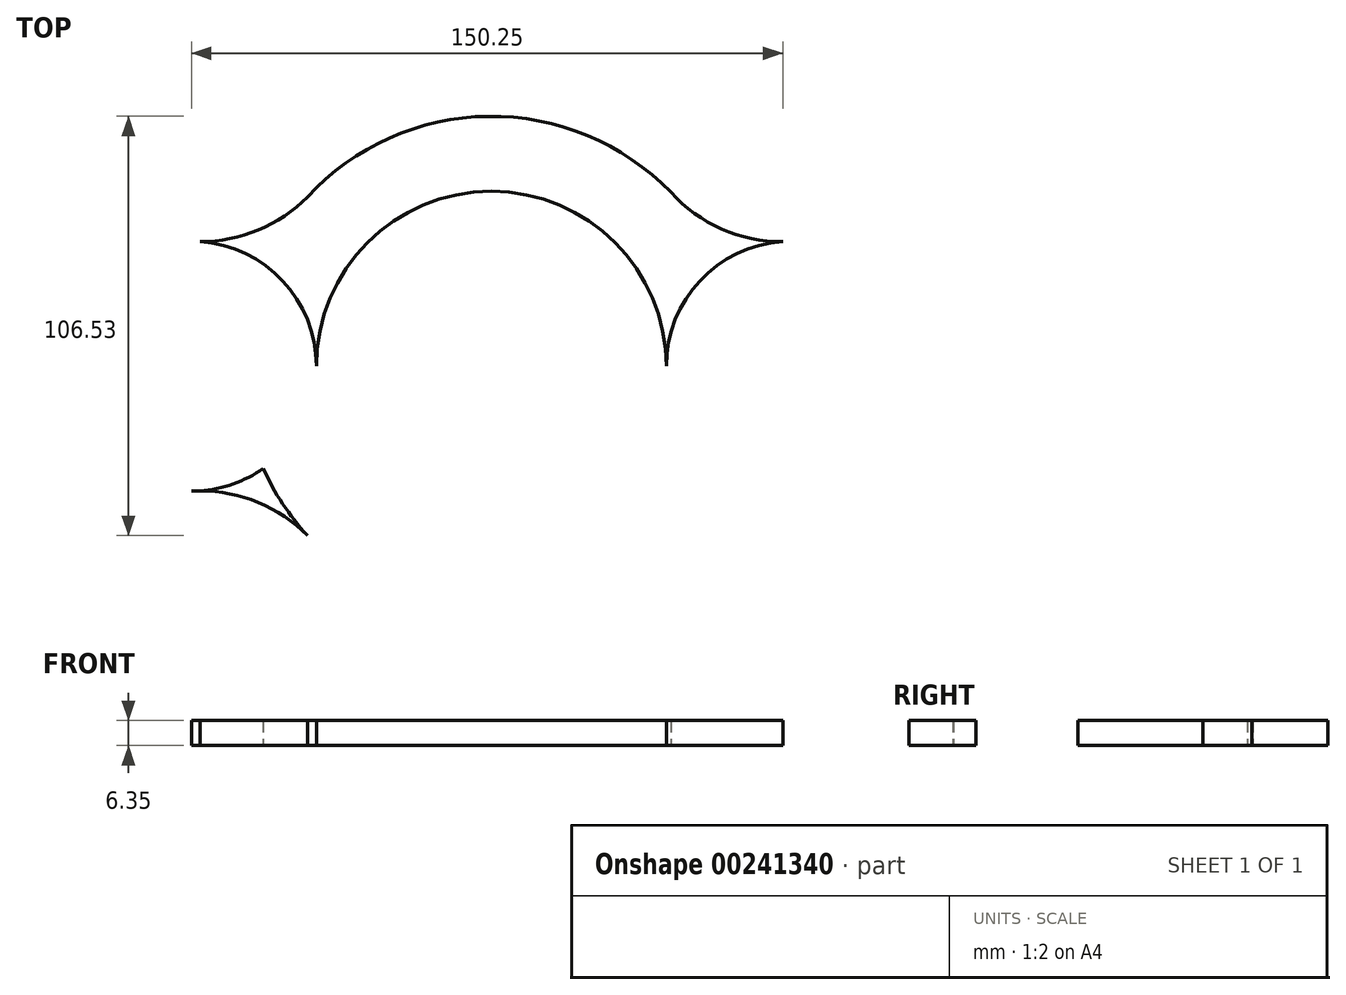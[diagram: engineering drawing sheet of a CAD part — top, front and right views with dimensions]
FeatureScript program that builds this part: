
annotation { "Feature Type Name" : "Feature", "Feature Type Description" : "" }
export const myFeature = defineFeature(function(context is Context, id is Id, definition is map)
    precondition{}
    {
        {
            var Q0;
            Q0=qCreatedBy(makeId("Top.planeOp"),FACE);
            var sketch = newSketch(context, id + "F0", { "sketchPlane" : qUnion([Q0])});
            skCircle(sketch, "E0", {"center": v(0, 0) * mm, "radius": 44.45 * mm});
            skCircle(sketch, "E1", {"center": v(0, 0) * mm, "radius": 63.5 * mm});
            skLineSegment(sketch, "E2", {"start": v(0, 0) * mm, "end": v(76.2, 0) * mm});
            skCircle(sketch, "E3", {"center": v(76.2, 0) * mm, "radius": 12.7 * mm});
            skCircle(sketch, "E4", {"center": v(76.2, 0) * mm, "radius": 31.75 * mm});
            skLineSegment(sketch, "E5", {"start": v(76.2, 0) * mm, "end": v(76.2, 31.75) * mm});
            skArc(sketch, "E6", {"start": v(45.6, 44.2) * mm, "mid": v(59.48, 34.48) * mm, "end": v(76.2, 31.75) * mm});
            skCircle(sketch, "E7.MirrorC", {"center": v(-76.2, 0) * mm, "radius": 12.7 * mm});
            skLineSegment(sketch, "E8.MirrorCS", {"start": v(-76.2, 0) * mm, "end": v(-76.2, 31.75) * mm});
            skLineSegment(sketch, "E9.MirrorCS", {"start": v(0, 0) * mm, "end": v(-76.2, 0) * mm});
            skArc(sketch, "E10.MirrorCS", {"start": v(-45.6, 44.2) * mm, "mid": v(-59.48, 34.48) * mm, "end": v(-76.2, 31.75) * mm});
            skCircle(sketch, "E11.MirrorC", {"center": v(-76.2, 0) * mm, "radius": 31.75 * mm});
            skArc(sketch, "E12.MirrorCS", {"start": v(45.6, 44.2) * mm, "mid": v(59.48, 34.48) * mm, "end": v(76.2, 31.75) * mm, "construction": true});
            skArc(sketch, "E13.MirrorCS", {"start": v(-45.6, -44.2) * mm, "mid": v(-59.48, -34.48) * mm, "end": v(-76.2, -31.75) * mm});
            skLineSegment(sketch, "E14.MirrorCS", {"start": v(-76.2, 0) * mm, "end": v(-76.2, -31.75) * mm});
            skArc(sketch, "E15.MirrorCS", {"start": v(45.6, -44.2) * mm, "mid": v(59.48, -34.48) * mm, "end": v(76.2, -31.75) * mm});
            skLineSegment(sketch, "E16.MirrorCS", {"start": v(76.2, 0) * mm, "end": v(76.2, -31.75) * mm});
            skSolve(sketch);
        }
        {
            var Q0;
            {var subQ0=sQuery(id+"F0.wireOp",EDGE,"E1");var subQ1=sQuery(id+"F0.wireOp",EDGE,"E6");var subQ2=makeQuery(id+"F0.imprint","INTERSECT",VERTEX,{"disambiguationData":[OD(1.0)],"derivedFrom":[subQ1,subQ0]});Q0=makeQuery(id+"F0.imprint","IMPRINT",FACE,{"disambiguationData":[TD([[makeQuery(id+"F0.imprint","IMPRINT",EDGE,{"disambiguationData":[TD([[subQ2,-1.0]])],"derivedFrom":subQ1}),-1.0]])]});}
            var Q1;
            {var subQ0=sQuery(id+"F0.wireOp",EDGE,"E4");var subQ5=sQuery(id+"F0.wireOp",EDGE,"E6");var subQ8=makeQuery(id+"F0.imprint","INTERSECT",VERTEX,{"derivedFrom":[subQ5,subQ0]});Q1=makeQuery(id+"F0.imprint","IMPRINT",FACE,{"disambiguationData":[TD([[makeQuery(id+"F0.imprint","IMPRINT",EDGE,{"disambiguationData":[TD([[subQ8,1.0]])],"derivedFrom":subQ0}),-1.0]])]});}
            var Q2;
            {var subQ1=sQuery(id+"F0.wireOp",EDGE,"E5");var subQ3=sQuery(id+"F0.wireOp",EDGE,"E3");var subQ4=makeQuery(id+"F0.imprint","INTERSECT",VERTEX,{"derivedFrom":[subQ1,subQ3]});Q2=makeQuery(id+"F0.imprint","IMPRINT",FACE,{"disambiguationData":[TD([[makeQuery(id+"F0.imprint","IMPRINT",EDGE,{"disambiguationData":[TD([[subQ4,-1.0]])],"derivedFrom":subQ3}),1.0]])]});}
            var Q3;
            {var subQ5=sQuery(id+"F0.wireOp",EDGE,"E4");var subQ6=sQuery(id+"F0.wireOp",EDGE,"E15.MirrorCS");var subQ8=makeQuery(id+"F0.imprint","INTERSECT",VERTEX,{"derivedFrom":[subQ6,subQ5]});Q3=makeQuery(id+"F0.imprint","IMPRINT",FACE,{"disambiguationData":[TD([[makeQuery(id+"F0.imprint","IMPRINT",EDGE,{"disambiguationData":[TD([[subQ8,-1.0]])],"derivedFrom":subQ5}),-1.0]])]});}
            var Q4;
            {var subQ0=sQuery(id+"F0.wireOp",EDGE,"E15.MirrorCS");var subQ1=sQuery(id+"F0.wireOp",EDGE,"E1");var subQ2=makeQuery(id+"F0.imprint","INTERSECT",VERTEX,{"disambiguationData":[OD(1.0)],"derivedFrom":[subQ1,subQ0]});Q4=makeQuery(id+"F0.imprint","IMPRINT",FACE,{"disambiguationData":[TD([[makeQuery(id+"F0.imprint","IMPRINT",EDGE,{"disambiguationData":[TD([[subQ2,1.0]])],"derivedFrom":subQ1}),1.0]])]});}
            var Q5;
            {var subQ1=sQuery(id+"F0.wireOp",EDGE,"E1");var subQ3=sQuery(id+"F0.wireOp",EDGE,"E15.MirrorCS");var subQ5=makeQuery(id+"F0.imprint","INTERSECT",VERTEX,{"disambiguationData":[OD(1.0)],"derivedFrom":[subQ1,subQ3]});Q5=makeQuery(id+"F0.imprint","IMPRINT",FACE,{"disambiguationData":[TD([[makeQuery(id+"F0.imprint","IMPRINT",EDGE,{"disambiguationData":[TD([[subQ5,1.0]])],"derivedFrom":subQ1}),-1.0]])]});}
            var Q6;
            {var subQ0=sQuery(id+"F0.wireOp",EDGE,"E4");var subQ1=sQuery(id+"F0.wireOp",EDGE,"E1");var subQ2=makeQuery(id+"F0.imprint","INTERSECT",VERTEX,{"disambiguationData":[OD(1.0)],"derivedFrom":[subQ1,subQ0]});Q6=makeQuery(id+"F0.imprint","IMPRINT",FACE,{"disambiguationData":[TD([[makeQuery(id+"F0.imprint","IMPRINT",EDGE,{"disambiguationData":[TD([[subQ2,1.0]])],"derivedFrom":subQ1}),-1.0]])]});}
            var Q7;
            {var subQ0=sQuery(id+"F0.wireOp",EDGE,"E4");var subQ1=sQuery(id+"F0.wireOp",EDGE,"E1");var subQ2=makeQuery(id+"F0.imprint","INTERSECT",VERTEX,{"disambiguationData":[OD(0.0)],"derivedFrom":[subQ1,subQ0]});Q7=makeQuery(id+"F0.imprint","IMPRINT",FACE,{"disambiguationData":[TD([[makeQuery(id+"F0.imprint","IMPRINT",EDGE,{"disambiguationData":[TD([[subQ2,-1.0]])],"derivedFrom":subQ1}),-1.0]])]});}
            var Q8;
            {var subQ0=sQuery(id+"F0.wireOp",EDGE,"E1");var subQ8=sQuery(id+"F0.wireOp",EDGE,"E6");var subQ9=makeQuery(id+"F0.imprint","INTERSECT",VERTEX,{"disambiguationData":[OD(0.0)],"derivedFrom":[subQ8,subQ0]});Q8=makeQuery(id+"F0.imprint","IMPRINT",FACE,{"disambiguationData":[TD([[makeQuery(id+"F0.imprint","IMPRINT",EDGE,{"disambiguationData":[TD([[subQ9,-1.0]])],"derivedFrom":subQ8}),-1.0]])]});}
            var Q9;
            {var subQ0=sQuery(id+"F0.wireOp",EDGE,"E1");var subQ1=sQuery(id+"F0.wireOp",EDGE,"E11.MirrorC");var subQ2=makeQuery(id+"F0.imprint","INTERSECT",VERTEX,{"disambiguationData":[OD(0.0)],"derivedFrom":[subQ1,subQ0]});Q9=makeQuery(id+"F0.imprint","IMPRINT",FACE,{"disambiguationData":[TD([[makeQuery(id+"F0.imprint","IMPRINT",EDGE,{"disambiguationData":[TD([[subQ2,-1.0]])],"derivedFrom":subQ1}),-1.0]])]});}
            var Q10;
            {var subQ0=sQuery(id+"F0.wireOp",EDGE,"E1");var subQ1=sQuery(id+"F0.wireOp",EDGE,"E11.MirrorC");var subQ2=makeQuery(id+"F0.imprint","INTERSECT",VERTEX,{"disambiguationData":[OD(1.0)],"derivedFrom":[subQ1,subQ0]});Q10=makeQuery(id+"F0.imprint","IMPRINT",FACE,{"disambiguationData":[TD([[makeQuery(id+"F0.imprint","IMPRINT",EDGE,{"disambiguationData":[TD([[subQ2,1.0]])],"derivedFrom":subQ1}),-1.0]])]});}
            var Q11;
            {var subQ1=sQuery(id+"F0.wireOp",EDGE,"E13.MirrorCS");var subQ2=sQuery(id+"F0.wireOp",EDGE,"E11.MirrorC");var subQ6=makeQuery(id+"F0.imprint","INTERSECT",VERTEX,{"derivedFrom":[subQ2,subQ1]});Q11=makeQuery(id+"F0.imprint","IMPRINT",FACE,{"disambiguationData":[TD([[makeQuery(id+"F0.imprint","IMPRINT",EDGE,{"disambiguationData":[TD([[subQ6,1.0]])],"derivedFrom":subQ2}),-1.0]])]});}
            var Q12;
            {var subQ0=sQuery(id+"F0.wireOp",EDGE,"E13.MirrorCS");var subQ1=sQuery(id+"F0.wireOp",EDGE,"E11.MirrorC");var subQ2=makeQuery(id+"F0.imprint","INTERSECT",VERTEX,{"derivedFrom":[subQ1,subQ0]});Q12=makeQuery(id+"F0.imprint","IMPRINT",FACE,{"disambiguationData":[TD([[makeQuery(id+"F0.imprint","IMPRINT",EDGE,{"disambiguationData":[TD([[subQ2,1.0]])],"derivedFrom":subQ1}),1.0]])]});}
            var Q13;
            {var subQ1=sQuery(id+"F0.wireOp",EDGE,"E8.MirrorCS");var subQ3=sQuery(id+"F0.wireOp",EDGE,"E7.MirrorC");var subQ4=makeQuery(id+"F0.imprint","INTERSECT",VERTEX,{"derivedFrom":[subQ1,subQ3]});Q13=makeQuery(id+"F0.imprint","IMPRINT",FACE,{"disambiguationData":[TD([[makeQuery(id+"F0.imprint","IMPRINT",EDGE,{"disambiguationData":[TD([[subQ4,-1.0]])],"derivedFrom":subQ3}),-1.0]])]});}
            var Q14;
            {var subQ1=sQuery(id+"F0.wireOp",EDGE,"E11.MirrorC");var subQ5=sQuery(id+"F0.wireOp",EDGE,"E10.MirrorCS");var subQ6=makeQuery(id+"F0.imprint","INTERSECT",VERTEX,{"derivedFrom":[subQ5,subQ1]});Q14=makeQuery(id+"F0.imprint","IMPRINT",FACE,{"disambiguationData":[TD([[makeQuery(id+"F0.imprint","IMPRINT",EDGE,{"disambiguationData":[TD([[subQ6,-1.0]])],"derivedFrom":subQ1}),-1.0]])]});}
            var Q15;
            {var subQ0=sQuery(id+"F0.wireOp",EDGE,"E1");var subQ1=sQuery(id+"F0.wireOp",EDGE,"E10.MirrorCS");var subQ2=makeQuery(id+"F0.imprint","INTERSECT",VERTEX,{"disambiguationData":[OD(1.0)],"derivedFrom":[subQ1,subQ0]});Q15=makeQuery(id+"F0.imprint","IMPRINT",FACE,{"disambiguationData":[TD([[makeQuery(id+"F0.imprint","IMPRINT",EDGE,{"disambiguationData":[TD([[subQ2,-1.0]])],"derivedFrom":subQ1}),1.0]])]});}
            extrude(context, id + "F1", {"entities" : qUnion([Q0, Q1, Q2, Q3, Q4, Q5, Q6, Q7, Q8, Q9, Q10, Q11, Q12, Q13, Q14, Q15]), "depth" : 6.35 * mm});
        }
    });
